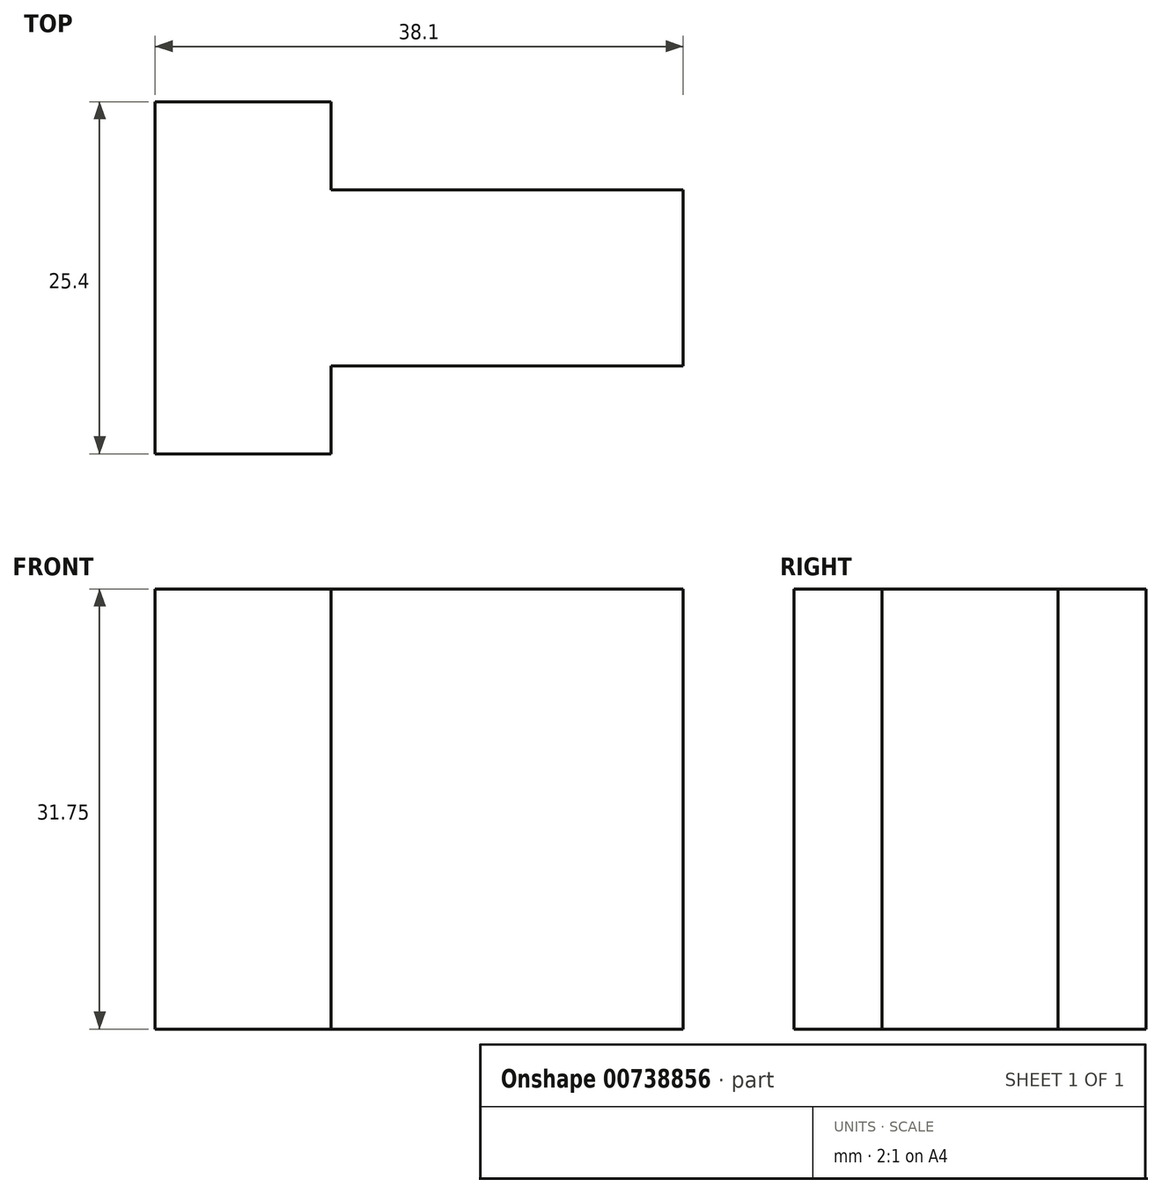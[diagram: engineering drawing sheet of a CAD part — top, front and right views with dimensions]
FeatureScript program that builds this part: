
annotation { "Feature Type Name" : "Feature", "Feature Type Description" : "" }
export const myFeature = defineFeature(function(context is Context, id is Id, definition is map)
    precondition{}
    {
        {
            var Q0;
            Q0=qCreatedBy(makeId("Front.planeOp"),FACE);
            var sketch = newSketch(context, id + "F0", { "sketchPlane" : qUnion([Q0])});
            skLineSegment(sketch, "E0", {"start": v(0, 31.75) * mm, "end": v(0, 0) * mm});
            skLineSegment(sketch, "E1", {"start": v(0, 0) * mm, "end": v(-38.1, 0) * mm});
            skLineSegment(sketch, "E2", {"start": v(0, 31.75) * mm, "end": v(-38.1, 31.75) * mm});
            skLineSegment(sketch, "E3", {"start": v(-38.1, 31.75) * mm, "end": v(-38.1, 0) * mm});
            skSolve(sketch);
        }
        {
            var Q0;
            Q0=makeQuery(id+"F0.imprint","IMPRINT",FACE,{"disambiguationData":[TD([[makeQuery(id+"F0.imprint","IMPRINT",EDGE,{"derivedFrom":sQuery(id+"F0.wireOp",EDGE,"E0")}),-1.0]])]});
            extrude(context, id + "F1", {"entities" : qUnion([Q0]), "depth" : 25.4 * mm, "offsetDistance" : 25.4 * mm});
        }
        {
            var Q0;
            Q0=makeQuery(id+"F1.opExtrude","SWEPT_FACE",FACE,{"disambiguationData":[OSD([sQuery(id+"F0.wireOp",EDGE,"E0")])]});
            var sketch = newSketch(context, id + "F2", { "sketchPlane" : qUnion([Q0])});
            skLineSegment(sketch, "E4", {"start": v(-19.05, 0) * mm, "end": v(-19.05, 31.75) * mm});
            skLineSegment(sketch, "E5", {"start": v(-19.05, 31.75) * mm, "end": v(-25.4, 31.75) * mm});
            skLineSegment(sketch, "E6", {"start": v(-25.05, 31.75) * mm, "end": v(-25.4, 0) * mm});
            skLineSegment(sketch, "E7", {"start": v(-25.4, 0.2) * mm, "end": v(-19.05, 0) * mm});
            skLineSegment(sketch, "E8", {"start": v(-6.35, 31.75) * mm, "end": v(-6.35, 0) * mm});
            skLineSegment(sketch, "E9", {"start": v(-6.35, 0) * mm, "end": v(0, 0) * mm});
            skLineSegment(sketch, "E10", {"start": v(0, 0) * mm, "end": v(-6.35, 0) * mm});
            skLineSegment(sketch, "E11", {"start": v(-6.35, 31.75) * mm, "end": v(0, 31.75) * mm});
            skLineSegment(sketch, "E12", {"start": v(0, 0) * mm, "end": v(0, 31.75) * mm});
            skLineSegment(sketch, "E13", {"start": v(0, 31.75) * mm, "end": v(-6.35, 31.75) * mm});
            skSolve(sketch);
        }
        {
            var Q0;
            Q0 = qSketchRegion(id + "F2", true);
            extrude(context, id + "F3", {"entities" : qUnion([Q0]), "operationType" : NewBodyOperationType.REMOVE, "oppositeDirection" : true, "depth" : 25.4 * mm, "offsetDistance" : 25.4 * mm});
        }
        {
            var Q0;
            Q0=makeQuery(id+"F1.opExtrude","CAP_FACE",FACE,{"disambiguationData":[OSD([sQuery(id+"F0.wireOp",EDGE,"E0"),sQuery(id+"F0.wireOp",EDGE,"E1"),sQuery(id+"F0.wireOp",EDGE,"E2"),sQuery(id+"F0.wireOp",EDGE,"E3")])],"isStart":false});
            var sketch = newSketch(context, id + "F4", { "sketchPlane" : qUnion([Q0])});
            skLineSegment(sketch, "E14", {"start": v(-25.4, 0) * mm, "end": v(-25.4, 31.75) * mm});
            skSolve(sketch);
        }
        {
            var Q0;
            {var subQ0=sQuery(id+"F4.wireOp",EDGE,"E14");Q0=makeQuery(id+"F4.imprint","IMPRINT",FACE,{"disambiguationData":[TD([[makeQuery(id+"F4.imprint","IMPRINT",EDGE,{"derivedFrom":subQ0}),-1.0]])]});}
            extrude(context, id + "F5", {"entities" : qUnion([Q0]), "operationType" : NewBodyOperationType.REMOVE, "oppositeDirection" : true, "depth" : 6.35 * mm, "offsetDistance" : 25.4 * mm});
        }
    });
